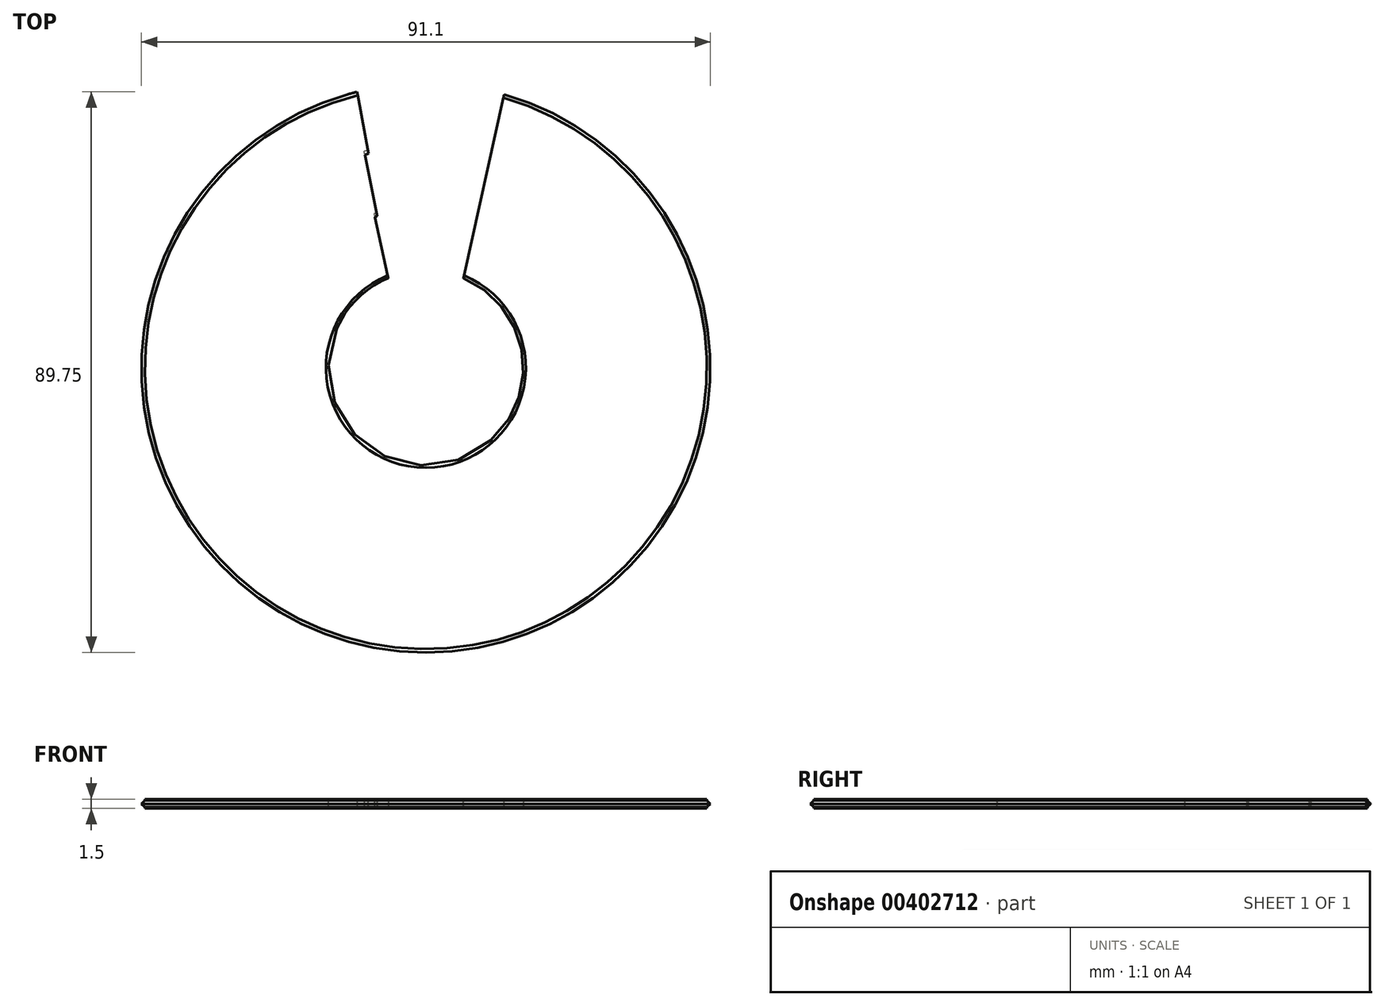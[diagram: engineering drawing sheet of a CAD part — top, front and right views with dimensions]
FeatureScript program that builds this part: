
annotation { "Feature Type Name" : "Feature", "Feature Type Description" : "" }
export const myFeature = defineFeature(function(context is Context, id is Id, definition is map)
    precondition{}
    {
        {
            var Q0;
            Q0=qCreatedBy(makeId("Front.planeOp"),FACE);
            var sketch = newSketch(context, id + "F0", { "sketchPlane" : qUnion([Q0])});
            skLineSegment(sketch, "E0", {"start": v(2.39, -1.74) * mm, "end": v(2.39, -1.43) * mm});
            skLineSegment(sketch, "E1", {"start": v(-45, 0.75) * mm, "end": v(-45, 0.55) * mm});
            skLineSegment(sketch, "E2", {"start": v(-45, 0.55) * mm, "end": v(-45.55, 0) * mm});
            skLineSegment(sketch, "E3", {"start": v(-45.55, 0) * mm, "end": v(-45, -0.55) * mm});
            skLineSegment(sketch, "E4", {"start": v(-45, -0.55) * mm, "end": v(-45, -0.75) * mm});
            skLineSegment(sketch, "E5", {"start": v(-45, -0.75) * mm, "end": v(-35, -0.75) * mm});
            skLineSegment(sketch, "E6", {"start": v(-35, -0.75) * mm, "end": v(-35, -0.55) * mm});
            skLineSegment(sketch, "E7", {"start": v(-35, -0.55) * mm, "end": v(-35.55, 0) * mm});
            skLineSegment(sketch, "E8", {"start": v(-35.55, 0) * mm, "end": v(-35, 0.55) * mm});
            skLineSegment(sketch, "E9", {"start": v(-35, 0.55) * mm, "end": v(-35, 0.75) * mm});
            skLineSegment(sketch, "E10", {"start": v(-35, 0.75) * mm, "end": v(-45, 0.75) * mm});
            skLineSegment(sketch, "E11", {"start": v(0, 0) * mm, "end": v(0, 16.96) * mm, "construction": true});
            skLineSegment(sketch, "E12", {"start": v(-35.5, 0.75) * mm, "end": v(-35.5, 0.55) * mm});
            skLineSegment(sketch, "E13", {"start": v(-35.5, 0.55) * mm, "end": v(-36.05, 0) * mm});
            skLineSegment(sketch, "E14", {"start": v(-36.05, 0) * mm, "end": v(-35.5, -0.55) * mm});
            skLineSegment(sketch, "E15", {"start": v(-35.5, -0.55) * mm, "end": v(-35.5, -0.75) * mm});
            skLineSegment(sketch, "E16", {"start": v(-35.5, -0.75) * mm, "end": v(-25.5, -0.75) * mm});
            skLineSegment(sketch, "E17", {"start": v(-25.5, -0.75) * mm, "end": v(-25.5, -0.55) * mm});
            skLineSegment(sketch, "E18", {"start": v(-25.5, -0.55) * mm, "end": v(-26.05, 0) * mm});
            skLineSegment(sketch, "E19", {"start": v(-26.05, 0) * mm, "end": v(-25.5, 0.55) * mm});
            skLineSegment(sketch, "E20", {"start": v(-25.5, 0.55) * mm, "end": v(-25.5, 0.75) * mm});
            skLineSegment(sketch, "E21", {"start": v(-25.5, 0.75) * mm, "end": v(-35.5, 0.75) * mm});
            skLineSegment(sketch, "E22", {"start": v(-26, 0.75) * mm, "end": v(-26, 0.55) * mm});
            skLineSegment(sketch, "E23", {"start": v(-26, 0.55) * mm, "end": v(-26.55, 0) * mm});
            skLineSegment(sketch, "E24", {"start": v(-26.55, 0) * mm, "end": v(-26, -0.55) * mm});
            skLineSegment(sketch, "E25", {"start": v(-26, -0.55) * mm, "end": v(-26, -0.75) * mm});
            skLineSegment(sketch, "E26", {"start": v(-26, -0.75) * mm, "end": v(-16, -0.75) * mm});
            skLineSegment(sketch, "E27", {"start": v(-16, 0.75) * mm, "end": v(-26, 0.75) * mm});
            skArc(sketch, "E28", {"start": v(-16, -0.75) * mm, "mid": v(-15.6, 0) * mm, "end": v(-16, 0.75) * mm});
            skSolve(sketch);
        }
        {
            var Q0;
            {var subQ2=sQuery(id+"F0.wireOp",EDGE,"E17");Q0=makeQuery(id+"F0.imprint","IMPRINT",FACE,{"disambiguationData":[TD([[makeQuery(id+"F0.imprint","IMPRINT",EDGE,{"derivedFrom":subQ2}),-1.0]])]});}
            var Q1;
            {var subQ1=sQuery(id+"F0.wireOp",EDGE,"E17");Q1=makeQuery(id+"F0.imprint","IMPRINT",FACE,{"disambiguationData":[TD([[makeQuery(id+"F0.imprint","IMPRINT",EDGE,{"derivedFrom":subQ1}),1.0]])]});}
            var Q2;
            Q2=sQuery(id+"F0.wireOp",EDGE,"E11");
            revolve(context, id + "F1", {"entities" : qUnion([Q0, Q1]), "axis" : qUnion([Q2]), "revolveType" : RevolveType.FULL});
        }
        {
            var Q0;
            {var subQ1=sQuery(id+"F0.wireOp",EDGE,"E6");Q0=makeQuery(id+"F0.imprint","IMPRINT",FACE,{"disambiguationData":[TD([[makeQuery(id+"F0.imprint","IMPRINT",EDGE,{"derivedFrom":subQ1}),-1.0]])]});}
            var Q1;
            {var subQ1=sQuery(id+"F0.wireOp",EDGE,"E17");Q1=makeQuery(id+"F0.imprint","IMPRINT",FACE,{"disambiguationData":[TD([[makeQuery(id+"F0.imprint","IMPRINT",EDGE,{"derivedFrom":subQ1}),1.0]])]});}
            var Q2;
            {var subQ1=sQuery(id+"F0.wireOp",EDGE,"E6");Q2=makeQuery(id+"F0.imprint","IMPRINT",FACE,{"disambiguationData":[TD([[makeQuery(id+"F0.imprint","IMPRINT",EDGE,{"derivedFrom":subQ1}),1.0]])]});}
            var Q3;
            Q3=sQuery(id+"F0.wireOp",EDGE,"E11");
            revolve(context, id + "F2", {"entities" : qUnion([Q0, Q1, Q2]), "axis" : qUnion([Q3]), "revolveType" : RevolveType.FULL});
        }
        {
            var Q0;
            Q0=makeQuery(id+"F0.imprint","IMPRINT",FACE,{"disambiguationData":[TD([[makeQuery(id+"F0.imprint","IMPRINT",EDGE,{"derivedFrom":sQuery(id+"F0.wireOp",EDGE,"E1")}),1.0]])]});
            var Q1;
            {var subQ1=sQuery(id+"F0.wireOp",EDGE,"E6");Q1=makeQuery(id+"F0.imprint","IMPRINT",FACE,{"disambiguationData":[TD([[makeQuery(id+"F0.imprint","IMPRINT",EDGE,{"derivedFrom":subQ1}),1.0]])]});}
            var Q2;
            Q2=sQuery(id+"F0.wireOp",EDGE,"E11");
            revolve(context, id + "F3", {"entities" : qUnion([Q0, Q1]), "axis" : qUnion([Q2]), "revolveType" : RevolveType.FULL});
        }
        {
            var Q0;
            Q0=makeQuery(id+"F1.opRevolve","SWEPT_FACE",FACE,{"disambiguationData":[OSD([sQuery(id+"F0.wireOp",EDGE,"E27")])]});
            var sketch = newSketch(context, id + "F4", { "sketchPlane" : qUnion([Q0])});
            skCircle(sketch, "E29", {"center": v(0, 0) * mm, "radius": 45.55 * mm, "construction": true});
            skLineSegment(sketch, "E30", {"start": v(-6, 14.3) * mm, "end": v(-12.54, 43.79) * mm});
            skLineSegment(sketch, "E31", {"start": v(12.54, 43.79) * mm, "end": v(6, 14.3) * mm});
            skLineSegment(sketch, "E32", {"start": v(0, 0) * mm, "end": v(0, 45.55) * mm, "construction": true});
            skArc(sketch, "E33", {"start": v(12.54, 43.79) * mm, "mid": v(0, 45.55) * mm, "end": v(-12.54, 43.79) * mm});
            skCircle(sketch, "E34", {"center": v(0, 0) * mm, "radius": 15.5 * mm});
            skSolve(sketch);
        }
        {
            var Q0;
            {var subQ0=sQuery(id+"F4.wireOp",EDGE,"E30");var subQ1=sQuery(id+"F0.wireOp",EDGE,"E27");var subQ2=makeQuery(id+"F1.opRevolve","SWEPT_EDGE",EDGE,{"disambiguationData":[OSD([sQuery(id+"F0.wireOp",EDGE,"bIvWAZmh-FEey-mwhQ-spOs-UgqX7yYtrs3j"),subQ1])]});var subQ3=makeQuery(id+"F4.imprint","INTERSECT",VERTEX,{"derivedFrom":[subQ2,subQ0]});Q0=makeQuery(id+"F4.imprint","IMPRINT",FACE,{"disambiguationData":[TD([[makeQuery(id+"F4.imprint","IMPRINT",EDGE,{"disambiguationData":[TD([[subQ3,-1.0]])],"derivedFrom":subQ0}),-1.0]])]});}
            var Q1;
            {var subQ0=sQuery(id+"F4.wireOp",EDGE,"E34");var subQ1=sQuery(id+"F4.wireOp",EDGE,"E30");var subQ2=makeQuery(id+"F4.imprint","INTERSECT",VERTEX,{"derivedFrom":[subQ1,subQ0]});Q1=makeQuery(id+"F4.imprint","IMPRINT",FACE,{"disambiguationData":[TD([[makeQuery(id+"F4.imprint","IMPRINT",EDGE,{"disambiguationData":[TD([[subQ2,1.0]])],"derivedFrom":subQ0}),-1.0]])]});}
            var Q2;
            {var subQ0=sQuery(id+"F4.wireOp",EDGE,"E33");Q2=makeQuery(id+"F4.imprint","IMPRINT",FACE,{"disambiguationData":[TD([[makeQuery(id+"F4.imprint","IMPRINT",EDGE,{"derivedFrom":subQ0}),1.0]])]});}
            var Q3;
            Q3=makeQuery(id+"F3.opRevolve","SWEPT_FACE",FACE,{"disambiguationData":[OSD([sQuery(id+"F0.wireOp",EDGE,"E5"),sQuery(id+"F0.wireOp",EDGE,"E16")])]});
            extrude(context, id + "F5", {"entities" : qUnion([Q0, Q1, Q2]), "operationType" : NewBodyOperationType.REMOVE, "endBound" : BoundingType.UP_TO_SURFACE, "oppositeDirection" : true, "endBoundEntityFace" : qUnion([Q3]), "depth" : 25 * mm});
        }
        {
            var Q0;
            Q0=makeQuery(id+"F5.boolean.opBoolean","COPY",FACE,{"disambiguationData":[TD([makeQuery(id+"F2.opRevolve","SWEPT_FACE",FACE,{"disambiguationData":[OSD([sQuery(id+"F0.wireOp",EDGE,"E12")])]})])],"derivedFrom":makeQuery(id+"F5.opExtrude","SWEPT_FACE",FACE,{"disambiguationData":[OSD([sQuery(id+"F4.wireOp",EDGE,"E30")])]})});
            var Q1;
            Q1=sQuery(id+"F0.wireOp",EDGE,"E11");
            revolve(context, id + "F6", {"operationType" : NewBodyOperationType.ADD, "entities" : qUnion([Q0]), "axis" : qUnion([Q1]), "revolveType" : RevolveType.ONE_DIRECTION, "oppositeDirection" : true, "angle" : 1 * degree});
        }
        {
            var Q0;
            Q0=makeQuery(id+"F5.boolean.opBoolean","COPY",FACE,{"disambiguationData":[TD([makeQuery(id+"F3.opRevolve","SWEPT_FACE",FACE,{"disambiguationData":[OSD([sQuery(id+"F0.wireOp",EDGE,"E1")])]})])],"derivedFrom":makeQuery(id+"F5.opExtrude","SWEPT_FACE",FACE,{"disambiguationData":[OSD([sQuery(id+"F4.wireOp",EDGE,"E30")])]})});
            var Q1;
            Q1=sQuery(id+"F0.wireOp",EDGE,"E11");
            revolve(context, id + "F7", {"operationType" : NewBodyOperationType.ADD, "entities" : qUnion([Q0]), "axis" : qUnion([Q1]), "revolveType" : RevolveType.ONE_DIRECTION, "oppositeDirection" : true, "angle" : 2 * degree});
        }
    });
